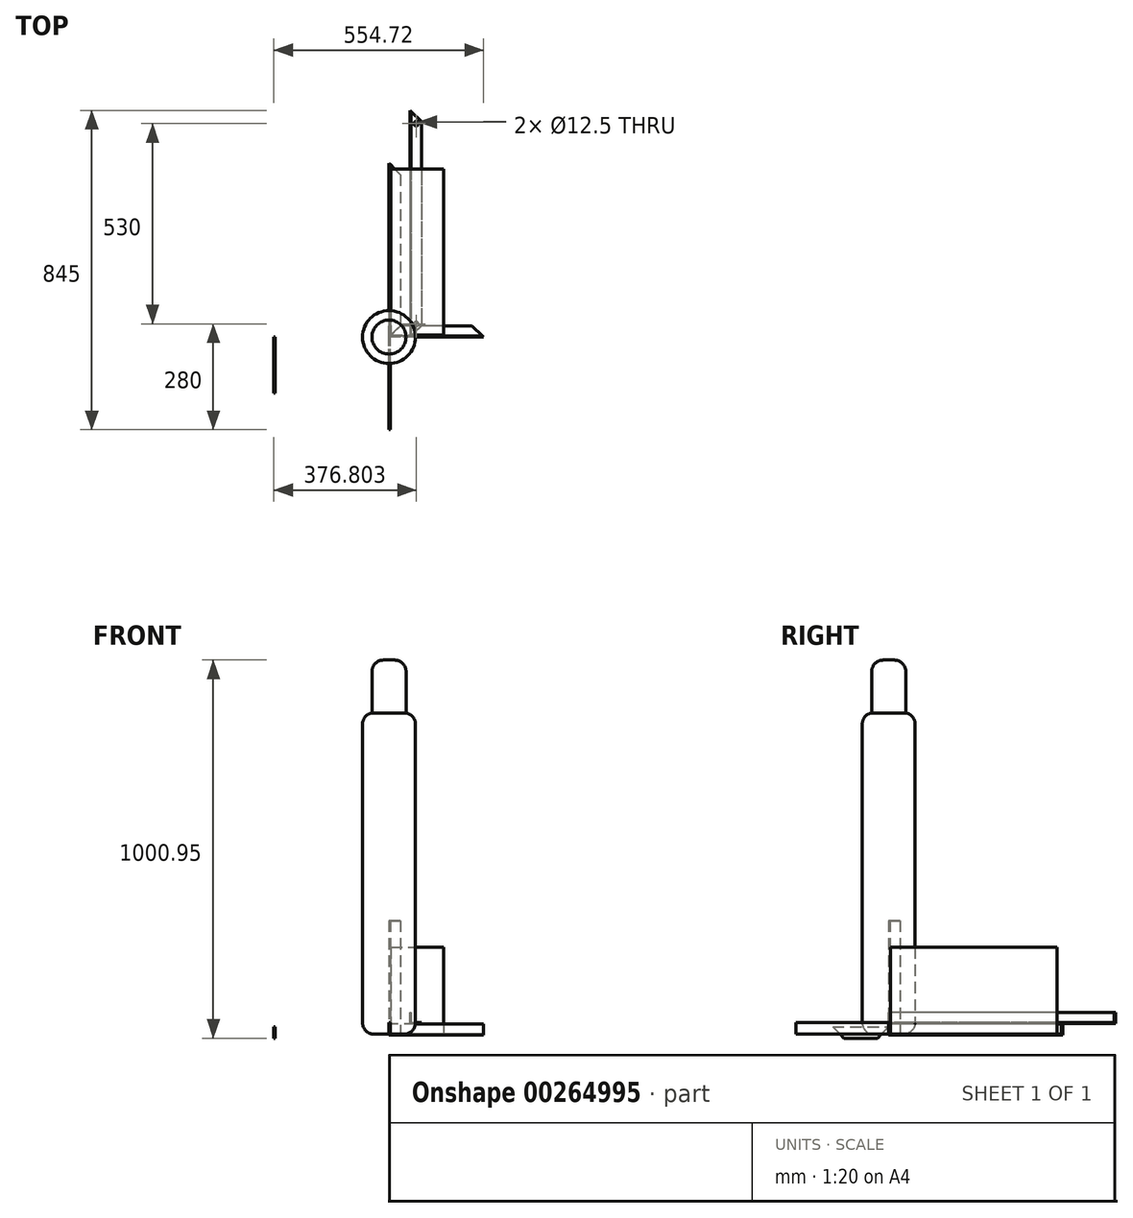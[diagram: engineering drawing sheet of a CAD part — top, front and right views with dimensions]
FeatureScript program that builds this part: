
annotation { "Feature Type Name" : "Feature", "Feature Type Description" : "" }
export const myFeature = defineFeature(function(context is Context, id is Id, definition is map)
    precondition{}
    {
        {
            var Q0;
            Q0=qCreatedBy(makeId("Top.planeOp"),FACE);
            var sketch = newSketch(context, id + "F0", { "sketchPlane" : qUnion([Q0])});
            skLineSegment(sketch, "E0.bottom", {"start": v(5, 445) * mm, "end": v(145, 445) * mm});
            skLineSegment(sketch, "E0.top", {"start": v(5, 5) * mm, "end": v(145, 5) * mm});
            skLineSegment(sketch, "E0.left", {"start": v(5, 445) * mm, "end": v(5, 5) * mm});
            skLineSegment(sketch, "E0.right", {"start": v(145, 445) * mm, "end": v(145, 5) * mm});
            skSolve(sketch);
        }
        {
            var Q0;
            Q0 = qSketchRegion(id + "F0", true);
            extrude(context, id + "F1", {"entities" : qUnion([Q0]), "depth" : 230 * mm});
        }
        {
            var Q0;
            Q0=qCreatedBy(makeId("Front.planeOp"),FACE);
            var sketch = newSketch(context, id + "F2", { "sketchPlane" : qUnion([Q0])});
            skLineSegment(sketch, "E1", {"start": v(3, 27) * mm, "end": v(3, 0) * mm});
            skLineSegment(sketch, "E2", {"start": v(3, 0) * mm, "end": v(30, 0) * mm});
            skLineSegment(sketch, "E3", {"start": v(30, 0) * mm, "end": v(30, -3) * mm});
            skLineSegment(sketch, "E4", {"start": v(30, -3) * mm, "end": v(0, -3) * mm});
            skLineSegment(sketch, "E5", {"start": v(0, -3) * mm, "end": v(0, 27) * mm});
            skLineSegment(sketch, "E6", {"start": v(0, 27) * mm, "end": v(3, 27) * mm});
            skSolve(sketch);
        }
        {
            var Q0;
            Q0 = qSketchRegion(id + "F2", true);
            extrude(context, id + "F3", {"entities" : qUnion([Q0]), "oppositeDirection" : true, "depth" : 460 * mm});
        }
        {
            var Q0;
            Q0=makeQuery(id+"F3.opExtrude","CAP_EDGE",EDGE,{"disambiguationData":[OSD([sQuery(id+"F2.wireOp",EDGE,"E3")])],"isStart":false});
            var Q1;
            Q1=makeQuery(id+"F3.opExtrude","CAP_EDGE",EDGE,{"disambiguationData":[OSD([sQuery(id+"F2.wireOp",EDGE,"E3")])],"isStart":true});
            chamfer(context, id + "F4", {"entities" : qUnion([Q0, Q1]), "width" : 30 * mm, "tangentPropagation" : true});
        }
        {
            var Q0;
            Q0=qCreatedBy(makeId("Right.planeOp"),FACE);
            var sketch = newSketch(context, id + "F5", { "sketchPlane" : qUnion([Q0])});
            skLineSegment(sketch, "E7", {"start": v(0, 27) * mm, "end": v(0, -3) * mm});
            skLineSegment(sketch, "E8", {"start": v(0, -3) * mm, "end": v(30, -3) * mm});
            skLineSegment(sketch, "E9", {"start": v(30, -3) * mm, "end": v(30, 0) * mm});
            skLineSegment(sketch, "E10", {"start": v(30, 0) * mm, "end": v(3, 0) * mm});
            skLineSegment(sketch, "E11", {"start": v(3, 0) * mm, "end": v(3, 27) * mm});
            skLineSegment(sketch, "E12", {"start": v(3, 27) * mm, "end": v(0, 27) * mm});
            skSolve(sketch);
        }
        {
            var Q0;
            Q0 = qSketchRegion(id + "F5", true);
            extrude(context, id + "F6", {"entities" : qUnion([Q0]), "depth" : 250 * mm});
        }
        {
            var Q0;
            Q0=makeQuery(id+"F6.opExtrude","CAP_EDGE",EDGE,{"disambiguationData":[OSD([sQuery(id+"F5.wireOp",EDGE,"E9")])],"isStart":true});
            var Q1;
            Q1=makeQuery(id+"F6.opExtrude","CAP_EDGE",EDGE,{"disambiguationData":[OSD([sQuery(id+"F5.wireOp",EDGE,"E9")])],"isStart":false});
            chamfer(context, id + "F7", {"entities" : qUnion([Q0, Q1]), "width" : 30 * mm, "tangentPropagation" : true});
        }
        {
            var Q0;
            Q0=qCreatedBy(makeId("Top.planeOp"),FACE);
            var sketch = newSketch(context, id + "F8", { "sketchPlane" : qUnion([Q0])});
            skLineSegment(sketch, "E13", {"start": v(0, 0) * mm, "end": v(0, 30) * mm});
            skLineSegment(sketch, "E14", {"start": v(0, 30) * mm, "end": v(3, 30) * mm});
            skLineSegment(sketch, "E15", {"start": v(3, 30) * mm, "end": v(3, 3) * mm});
            skLineSegment(sketch, "E16", {"start": v(3, 3) * mm, "end": v(30, 3) * mm});
            skLineSegment(sketch, "E17", {"start": v(30, 3) * mm, "end": v(30, 0) * mm});
            skLineSegment(sketch, "E18", {"start": v(30, 0) * mm, "end": v(0, 0) * mm});
            skLineSegment(sketch, "E19", {"start": v(0, 0) * mm, "end": v(30, 0) * mm});
            skSolve(sketch);
        }
        {
            var Q0;
            Q0 = qSketchRegion(id + "F8", true);
            extrude(context, id + "F9", {"entities" : qUnion([Q0]), "depth" : 300 * mm});
        }
        {
            var Q0;
            Q0=qCreatedBy(makeId("Front.planeOp"),FACE);
            var sketch = newSketch(context, id + "F10", { "sketchPlane" : qUnion([Q0])});
            skLineSegment(sketch, "E20", {"start": v(58.58, 57.59) * mm, "end": v(58.58, 30.59) * mm});
            skLineSegment(sketch, "E21", {"start": v(58.58, 30.59) * mm, "end": v(85.58, 30.59) * mm});
            skLineSegment(sketch, "E22", {"start": v(85.58, 30.59) * mm, "end": v(85.58, 27.59) * mm});
            skLineSegment(sketch, "E23", {"start": v(85.58, 27.59) * mm, "end": v(55.58, 27.59) * mm});
            skLineSegment(sketch, "E24", {"start": v(55.58, 27.59) * mm, "end": v(55.58, 57.59) * mm});
            skLineSegment(sketch, "E25", {"start": v(55.58, 57.59) * mm, "end": v(58.58, 57.59) * mm});
            skSolve(sketch);
        }
        {
            var Q0;
            Q0 = qSketchRegion(id + "F10", true);
            extrude(context, id + "F11", {"entities" : qUnion([Q0]), "oppositeDirection" : true, "depth" : (450 + 150) * mm});
        }
        {
            var Q0;
            Q0=makeQuery(id+"F11.opExtrude","CAP_EDGE",EDGE,{"disambiguationData":[OSD([sQuery(id+"F10.wireOp",EDGE,"E22")])],"isStart":true});
            var Q1;
            Q1=makeQuery(id+"F11.opExtrude","CAP_EDGE",EDGE,{"disambiguationData":[OSD([sQuery(id+"F10.wireOp",EDGE,"E22")])],"isStart":false});
            chamfer(context, id + "F12", {"entities" : qUnion([Q0, Q1]), "width" : 30 * mm, "tangentPropagation" : true});
        }
        {
            var Q0;
            Q0=qCreatedBy(makeId("Front.planeOp"),FACE);
            var sketch = newSketch(context, id + "F13", { "sketchPlane" : qUnion([Q0])});
            skLineSegment(sketch, "E26.bottom", {"start": v(0, 0) * mm, "end": v(3, 0) * mm});
            skLineSegment(sketch, "E26.top", {"start": v(0, 30) * mm, "end": v(3, 30) * mm});
            skLineSegment(sketch, "E26.left", {"start": v(0, 0) * mm, "end": v(0, 30) * mm});
            skLineSegment(sketch, "E26.right", {"start": v(3, 0) * mm, "end": v(3, 30) * mm});
            skSolve(sketch);
        }
        {
            var Q0;
            Q0 = qSketchRegion(id + "F13", true);
            extrude(context, id + "F14", {"entities" : qUnion([Q0]), "depth" : 245 * mm});
        }
        {
            var Q0;
            Q0=qCreatedBy(makeId("Front.planeOp"),FACE);
            var sketch = newSketch(context, id + "F15", { "sketchPlane" : qUnion([Q0])});
            skLineSegment(sketch, "E27.bottom", {"start": v(-304.72, -10.95) * mm, "end": v(-301.72, -10.95) * mm});
            skLineSegment(sketch, "E27.top", {"start": v(-304.72, 19.05) * mm, "end": v(-301.72, 19.05) * mm});
            skLineSegment(sketch, "E27.left", {"start": v(-304.72, -10.95) * mm, "end": v(-304.72, 19.05) * mm});
            skLineSegment(sketch, "E27.right", {"start": v(-301.72, -10.95) * mm, "end": v(-301.72, 19.05) * mm});
            skSolve(sketch);
        }
        {
            var Q0;
            Q0 = qSketchRegion(id + "F15", true);
            extrude(context, id + "F16", {"entities" : qUnion([Q0]), "depth" : 148 * mm});
        }
        {
            var Q0;
            Q0=makeQuery(id+"F16.opExtrude","CAP_EDGE",EDGE,{"disambiguationData":[OSD([sQuery(id+"F15.wireOp",EDGE,"E27.bottom")])],"isStart":true});
            var Q1;
            Q1=makeQuery(id+"F16.opExtrude","CAP_EDGE",EDGE,{"disambiguationData":[OSD([sQuery(id+"F15.wireOp",EDGE,"E27.bottom")])],"isStart":false});
            chamfer(context, id + "F17", {"entities" : qUnion([Q0, Q1]), "width" : 30 * mm, "tangentPropagation" : true});
        }
        {
            var Q0;
            Q0=makeQuery(id+"F11.opExtrude","SWEPT_FACE",FACE,{"disambiguationData":[OSD([sQuery(id+"F10.wireOp",EDGE,"E21")])]});
            var sketch = newSketch(context, id + "F18", { "sketchPlane" : qUnion([Q0])});
            skPoint(sketch, "E28", {"position": v(72.08, 565) * mm});
            skPoint(sketch, "E28.positionSnap0", {"position": v(72.08, 583.5) * mm});
            skPoint(sketch, "E29", {"position": v(72.08, 35) * mm});
            skPoint(sketch, "E29.positionSnap0", {"position": v(72.08, 16.5) * mm});
            skSolve(sketch);
        }
        {
            var Q0;
            Q0=sQuery(id+"F18.wireOp",VERTEX,"E29");
            var Q1;
            Q1=sQuery(id+"F18.wireOp",VERTEX,"E28");
            var Q2;
            Q2=makeQuery(id+"F6.opExtrude","SWEPT_BODY",BODY,{"disambiguationData":[OSD([sQuery(id+"F5.wireOp",EDGE,"E7"),sQuery(id+"F5.wireOp",EDGE,"E8"),sQuery(id+"F5.wireOp",EDGE,"E9"),sQuery(id+"F5.wireOp",EDGE,"E10"),sQuery(id+"F5.wireOp",EDGE,"E11"),sQuery(id+"F5.wireOp",EDGE,"E12")])]});
            var Q3;
            Q3=makeQuery(id+"F11.opExtrude","SWEPT_BODY",BODY,{"disambiguationData":[OSD([sQuery(id+"F10.wireOp",EDGE,"E20"),sQuery(id+"F10.wireOp",EDGE,"E21"),sQuery(id+"F10.wireOp",EDGE,"E22"),sQuery(id+"F10.wireOp",EDGE,"E23"),sQuery(id+"F10.wireOp",EDGE,"E24"),sQuery(id+"F10.wireOp",EDGE,"E25")])]});
            hole(context, id + "F19", {"style" : HoleStyle.SIMPLE, "endStyle" : HoleEndStyle.THROUGH, "holeDiameter" : 12.5 * mm, "tappedDepth" : 12 * mm, "tapClearance" : 3, "locations" : qUnion([Q0, Q1]), "scope" : qUnion([Q2, Q3])});
        }
        {
            var Q0;
            Q0=qCreatedBy(makeId("Top.planeOp"),FACE);
            var sketch = newSketch(context, id + "F20", { "sketchPlane" : qUnion([Q0])});
            skCircle(sketch, "E30", {"center": v(0, 0) * mm, "radius": 70 * mm});
            skSolve(sketch);
        }
        {
            var Q0;
            Q0 = qSketchRegion(id + "F20", true);
            extrude(context, id + "F21", {"entities" : qUnion([Q0]), "depth" : 850 * mm});
        }
        {
            var Q0;
            Q0=makeQuery(id+"F21.opExtrude","CAP_FACE",FACE,{"disambiguationData":[OSD([sQuery(id+"F20.wireOp",EDGE,"E30")])],"isStart":false});
            var sketch = newSketch(context, id + "F22", { "sketchPlane" : qUnion([Q0])});
            skCircle(sketch, "E31", {"center": v(0, 0) * mm, "radius": 45 * mm});
            skSolve(sketch);
        }
        {
            var Q0;
            Q0 = qSketchRegion(id + "F22", true);
            extrude(context, id + "F23", {"entities" : qUnion([Q0]), "operationType" : NewBodyOperationType.ADD, "depth" : (990 - 850) * mm});
        }
        {
            var Q0;
            Q0=makeQuery(id+"F21.opExtrude","CAP_EDGE",EDGE,{"disambiguationData":[OSD([sQuery(id+"F20.wireOp",EDGE,"E30")])],"isStart":true});
            var Q1;
            Q1=makeQuery(id+"F21.opExtrude","CAP_EDGE",EDGE,{"disambiguationData":[OSD([sQuery(id+"F20.wireOp",EDGE,"E30")])],"isStart":false});
            var Q2;
            Q2=makeQuery(id+"F23.opExtrude","CAP_EDGE",EDGE,{"disambiguationData":[OSD([sQuery(id+"F22.wireOp",EDGE,"E31")])],"isStart":false});
            fillet(context, id + "F24", {"entities" : qUnion([Q0, Q1, Q2]), "radius" : 30 * mm, "tangentPropagation" : true, "allowEdgeOverflow" : false});
        }
    });
